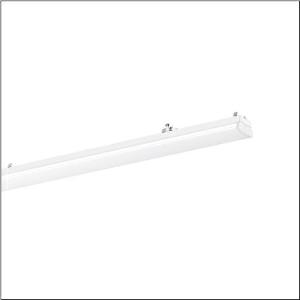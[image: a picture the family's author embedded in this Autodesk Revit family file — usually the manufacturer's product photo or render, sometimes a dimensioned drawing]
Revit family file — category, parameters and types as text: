
# Revit family: licross_r__11_recessed_opal_ho_51tl1dmn4d5m_ffb9
name_source: partatom
category: Lighting Fixtures
units: mm (PartAtom-declared; Revit-internal decimal feet)

## family parameters
Cut with Voids When Loaded = No
Host = Face
Light Source = No
Part Type = Normal
Room Calculation Point = No
Round Connector Dimension = Use Diameter
Shared = No

## types (1)
- --- (1 x LED, 13690 lm, 74.5 W, 4000K)
    Apparent Load = 75 VA
    CIE Flux Codes = 44 73 91 87 100
    Color Rendering = 80
    Color Temperature = 4000K
    Default Elevation = 1800 mm
    Description = Licross® 11 recessed opal HO, luminaire insert, of sheet steel, coil coated, white, length: 1.500mm, width: 76mm, height: 87mm, LED rated luminous flux: 13.690lm, light colour: 840, control gear: ON/OFF Multilumen, with plug, 3-pole, with phase selection, mains connection: 220..240V, AC, 50/60Hz, rated input power: 75W, halogen-free wiring, primary optical cover: cover, of PMMA, light emission: direct with ceiling illumination distribution, primary light characteristic: symmetric, protection rating (complete): IP40, insulation class (complete): insulation class I (protective earthing), certification: CE, ENEC, VDE, UKCA, protection symbol: D if used in an environment without relevant dust loads with corresponding accessories, impact resistance: IK06, permissible ambient temperature for indoor applications: -35..+35°C, corresponds to IFS (International Featured Standards) requirements for safety and quality in the food industry, reducing of maximum allowable ambient temperature of 5°C with ceiling mounting, packaging unit: 1 piece
    Height = 83 mm
    Lamp = 1 x LED
    Lamp Light Flux = 13690 lm
    Lamp Power = 74.5 W
    Lamp count = 1
    Length = 1500 mm
    Luminous efficacy = 184 lm/W
    Manufacturer = Siteco
    ModVariant = No
    Model = 51TL1DMN4D5M
    Mounting Place = Ceiling
    Mounting Type = Pendant
    Number of Poles = 1
    OnlyDefault = Yes
    Power Factor = 1
    Product Name = Licross® 11 recessed opal HO
    Product group = luminaire insert
    ProductGroupID = 901
    Protection Class = Protection class I
    Protection Degree = IP 40
    RLX_Detail_Level = 1
    RLX_Emergency_Light_Flux = 0 lm
    RLX_Emergency_Type = 0
    RLX_Emergency_Type_DB = No
    RlxData = <blob elided: 24565 chars, md5=9027cac6>
    Socket = socket
    Standby Power = 0 W
    System Light Flux = 13690 lm
    System Power = 75 W
    Type Comments = factory setting: luminous flux: 100 % | (A | C | E) | 174 mA
    Type Image = l_1313666.jpg
    URL = http://relux.com
    VarID = @adj_044789
    Voltage = 0 V
    Weight = 0.00 kg
    Width = 76 mm

## geometry (parser evidence)
native form markers: Blend x4, Sweep x12
no freeform markers — native parametric forms only
